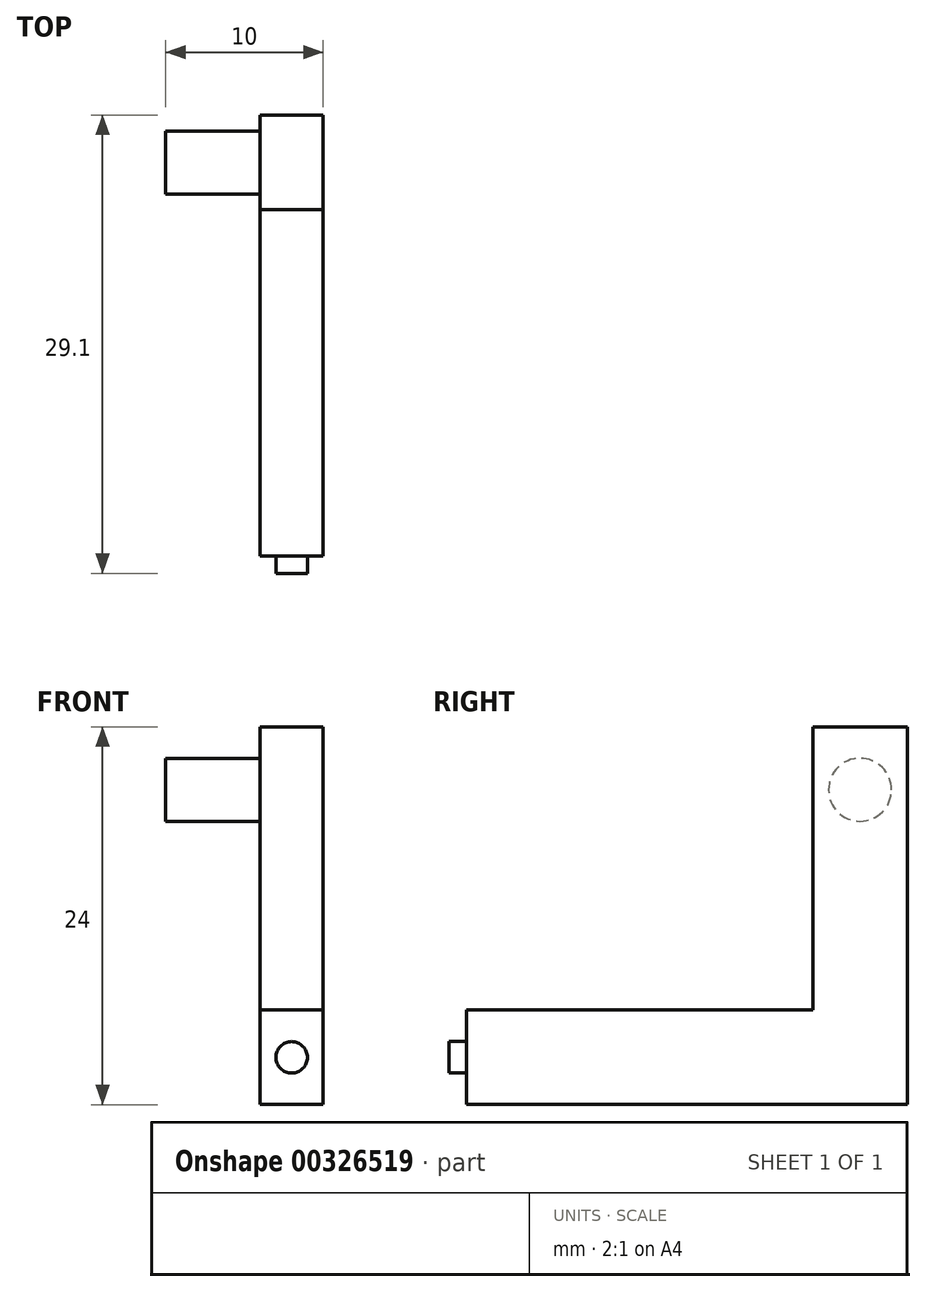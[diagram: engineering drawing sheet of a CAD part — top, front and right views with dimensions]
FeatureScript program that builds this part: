
annotation { "Feature Type Name" : "Feature", "Feature Type Description" : "" }
export const myFeature = defineFeature(function(context is Context, id is Id, definition is map)
    precondition{}
    {
        {
            var Q0;
            Q0=qCreatedBy(makeId("Front.planeOp"),FACE);
            var sketch = newSketch(context, id + "F0", { "sketchPlane" : qUnion([Q0])});
            skLineSegment(sketch, "E0", {"start": v(-2, 21.8) * mm, "end": v(2, 21.8) * mm});
            skLineSegment(sketch, "E1", {"start": v(-2, 21.8) * mm, "end": v(-2, -2.2) * mm});
            skLineSegment(sketch, "E2", {"start": v(-2, -2.2) * mm, "end": v(2, -2.2) * mm});
            skLineSegment(sketch, "E3", {"start": v(2, -2.2) * mm, "end": v(2, 21.8) * mm});
            skLineSegment(sketch, "E4", {"start": v(-2, 3.8) * mm, "end": v(2, 3.8) * mm});
            skSolve(sketch);
        }
        {
            var Q0;
            {var subQ0=sQuery(id+"F0.wireOp",EDGE,"E0");Q0=makeQuery(id+"F0.imprint","IMPRINT",FACE,{"disambiguationData":[TD([[makeQuery(id+"F0.imprint","IMPRINT",EDGE,{"derivedFrom":subQ0}),-1.0]])]});}
            extrude(context, id + "F1", {"entities" : qUnion([Q0]), "depth" : 6 * mm});
        }
        {
            var Q0;
            {var subQ0=sQuery(id+"F0.wireOp",EDGE,"E2");Q0=makeQuery(id+"F0.imprint","IMPRINT",FACE,{"disambiguationData":[TD([[makeQuery(id+"F0.imprint","IMPRINT",EDGE,{"derivedFrom":subQ0}),1.0]])]});}
            extrude(context, id + "F2", {"entities" : qUnion([Q0]), "operationType" : NewBodyOperationType.ADD, "depth" : 28 * mm});
        }
        {
            var Q0;
            Q0=makeQuery(id+"F2.opExtrude","CAP_FACE",FACE,{"disambiguationData":[OSD([sQuery(id+"F0.wireOp",EDGE,"E1"),sQuery(id+"F0.wireOp",EDGE,"E2"),sQuery(id+"F0.wireOp",EDGE,"E3"),sQuery(id+"F0.wireOp",EDGE,"E4")])],"isStart":false});
            var sketch = newSketch(context, id + "F3", { "sketchPlane" : qUnion([Q0])});
            skCircle(sketch, "E5", {"center": v(0, 0.8) * mm, "radius": 1 * mm});
            skSolve(sketch);
        }
        {
            var Q0;
            Q0=makeQuery(id+"F3.imprint","IMPRINT",FACE,{"disambiguationData":[TD([[makeQuery(id+"F3.imprint","IMPRINT",EDGE,{"derivedFrom":sQuery(id+"F3.wireOp",EDGE,"E5")}),1.0]])]});
            extrude(context, id + "F4", {"entities" : qUnion([Q0]), "operationType" : NewBodyOperationType.ADD, "depth" : 1.1 * mm});
        }
        {
            var Q0;
            {var subQ0=sQuery(id+"F0.wireOp",EDGE,"E1");Q0=makeQuery(id+"F2.boolean.opBoolean","MERGE",FACE,{"derivedFrom":[makeQuery(id+"F1.opExtrude","SWEPT_FACE",FACE,{"disambiguationData":[OSD([subQ0])]}),makeQuery(id+"F2.opExtrude","SWEPT_FACE",FACE,{"disambiguationData":[OSD([subQ0])]})]});}
            var sketch = newSketch(context, id + "F5", { "sketchPlane" : qUnion([Q0])});
            skCircle(sketch, "E6", {"center": v(3, 17.8) * mm, "radius": 2 * mm});
            skSolve(sketch);
        }
        {
            var Q0;
            Q0=makeQuery(id+"F5.imprint","IMPRINT",FACE,{"disambiguationData":[TD([[makeQuery(id+"F5.imprint","IMPRINT",EDGE,{"derivedFrom":sQuery(id+"F5.wireOp",EDGE,"E6")}),1.0]])]});
            extrude(context, id + "F6", {"entities" : qUnion([Q0]), "operationType" : NewBodyOperationType.ADD, "depth" : 6 * mm});
        }
    });
